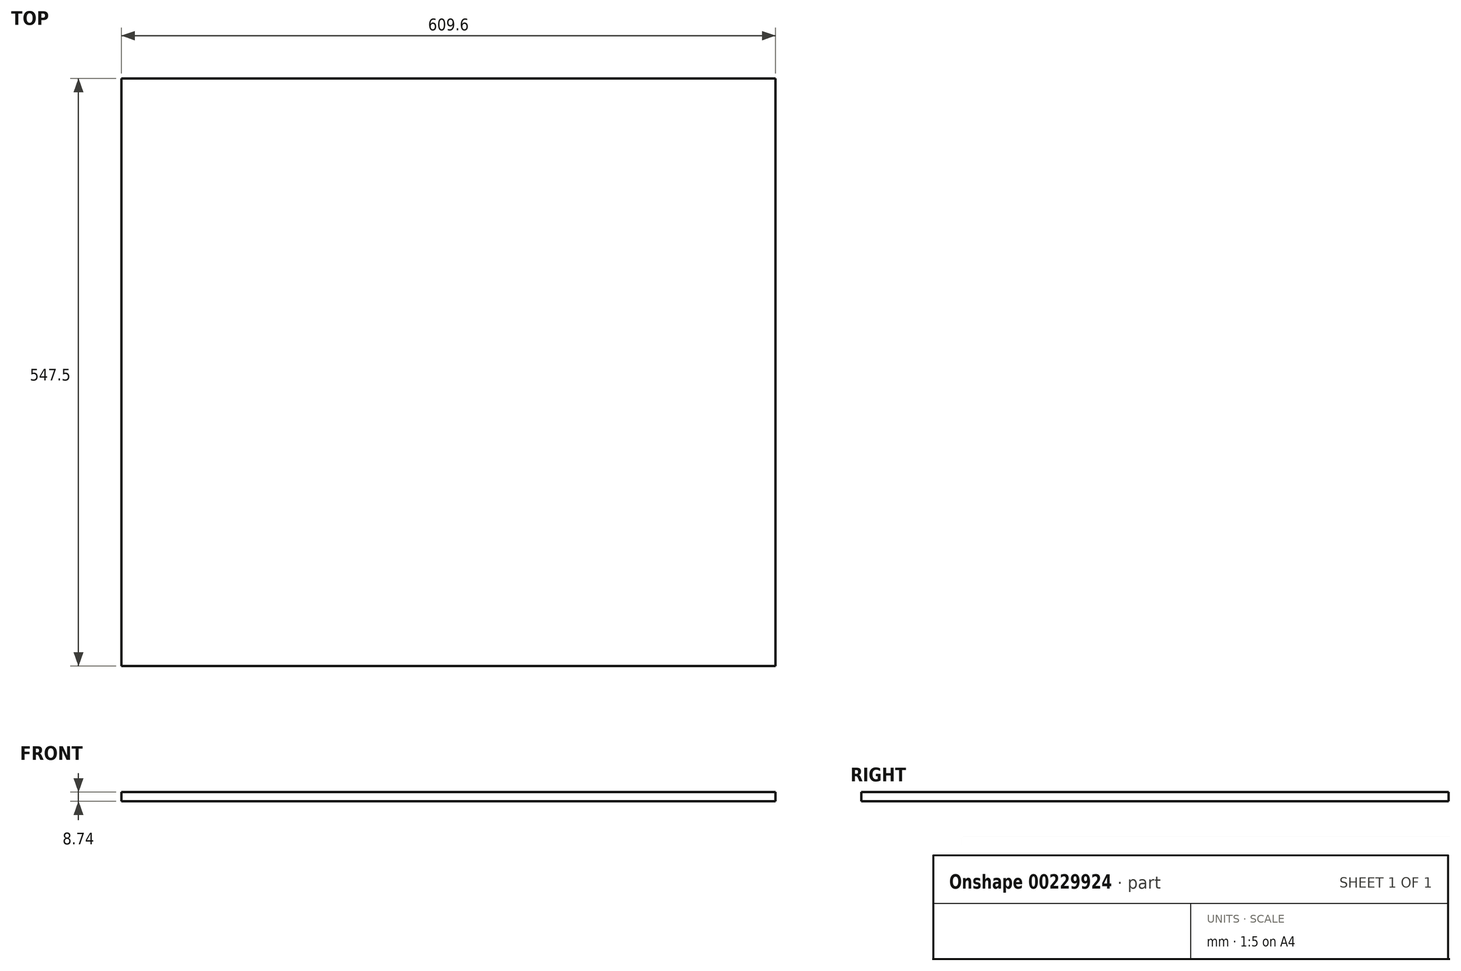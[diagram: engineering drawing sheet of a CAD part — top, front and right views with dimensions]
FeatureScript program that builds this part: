
annotation { "Feature Type Name" : "Feature", "Feature Type Description" : "" }
export const myFeature = defineFeature(function(context is Context, id is Id, definition is map)
    precondition{}
    {
        {
            var Q0;
            Q0=qCreatedBy(makeId("Top.planeOp"),FACE);
            var sketch = newSketch(context, id + "F0", { "sketchPlane" : qUnion([Q0])});
            skLineSegment(sketch, "E0.bottom", {"start": v(-304.8, 273.75) * mm, "end": v(304.8, 273.75) * mm});
            skLineSegment(sketch, "E0.top", {"start": v(-304.8, -273.75) * mm, "end": v(304.8, -273.75) * mm});
            skLineSegment(sketch, "E0.left", {"start": v(-304.8, 273.75) * mm, "end": v(-304.8, -273.75) * mm});
            skLineSegment(sketch, "E0.right", {"start": v(304.8, 273.75) * mm, "end": v(304.8, -273.75) * mm});
            skLineSegment(sketch, "E1", {"start": v(-304.8, 273.75) * mm, "end": v(304.8, -273.75) * mm, "construction": true});
            skSolve(sketch);
        }
        {
            var Q0;
            Q0=makeQuery(id+"F0.imprint","IMPRINT",FACE,{"disambiguationData":[TD([[makeQuery(id+"F0.imprint","IMPRINT",EDGE,{"derivedFrom":sQuery(id+"F0.wireOp",EDGE,"E0.bottom")}),-1.0]])]});
            extrude(context, id + "F1", {"entities" : qUnion([Q0]), "depth" : 8.74 * mm});
        }
    });
